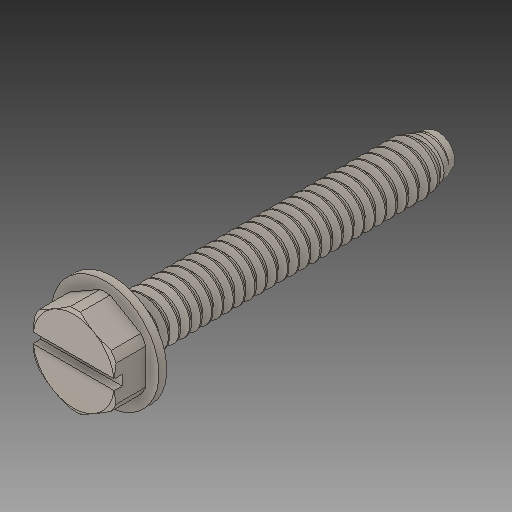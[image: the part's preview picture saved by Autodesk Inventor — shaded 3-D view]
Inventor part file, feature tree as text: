
AUTODESK INVENTOR PART (.ipt)
format: ipt  version: 2018 (Build 220112000, 112)  size: 532,992 bytes
history: native  units: in
note: dims shown in document units (in); Inventor stores cm internally (conversion verified against a paired STEP export)
features: extrude x1
ambient origin geometry x8: Origin, YZ Plane, XZ Plane, XY Plane, X Axis, Y Axis, Z Axis, Center Point
bodies: Solid1 (feature_tree)
feature tree (1):
  extrude  "Extrude4"  [1 undecoded]
note: 1 required parameter value undecoded (feature->parameter linkage not recoverable at this tier; creation-order binding heuristic only, values carry confidence <= 0.55)
